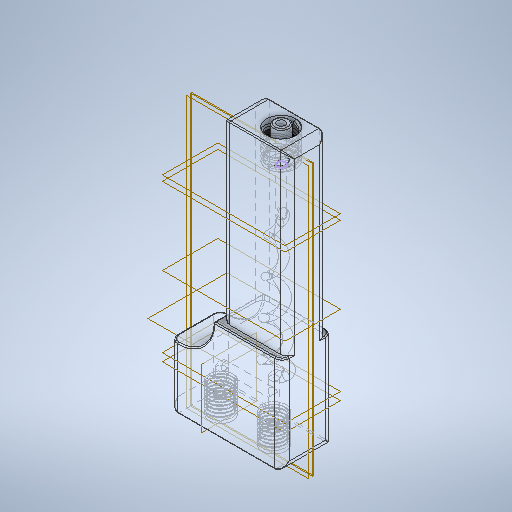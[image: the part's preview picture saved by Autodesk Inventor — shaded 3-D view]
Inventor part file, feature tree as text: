
AUTODESK INVENTOR PART (.ipt)
format: ipt  version: 2025 (Build 290162000, 162)  size: 1,340,416 bytes
history: native  units: mm
features: sketch x25, extrude x14, plane x11, other x7, revolve x6, fillet x3, projected_geometry x1
ambient origin geometry x8: Origin, YZ Plane, XZ Plane, XY Plane, X Axis, Y Axis, Z Axis, Center Point
bodies: Volumenkörper1 (feature_tree), Volumenkörper4 (feature_tree), Volumenkörper5 (feature_tree)
feature tree (67):
  extrude  "Extrusion1"  Depth=14.0mm
  extrude  "Extrusion2"  Depth=6.584mm
  plane  "Arbeitsebene4"
  extrude  "Extrusion3"  Depth=2.2mm
  extrude  "Extrusion8"  TaperAngle=0.0deg  [1 undecoded]
  revolve  "Umdrehung3"
  plane  "Arbeitsebene12"
  extrude  "Extrusion10"  Depth=5.0mm TaperAngle=0.0deg
  plane  "Arbeitsebene7"
  extrude  "Extrusion13"  Depth=2.2mm TaperAngle=0.0deg
  extrude  "Extrusion14"  Depth=2.8mm TaperAngle=0.0deg
  other  "Spirale2"
  revolve  "Umdrehung9"
  extrude  "Extrusion15"  Depth=11.0mm
  revolve  "Umdrehung10"
  extrude  "Extrusion16"  Depth=50.0mm TaperAngle=0.0deg
  sketch  "Skizze32"  dims[d91=5.818mm d92=8.0mm d93=-0.061087mm]
  plane  "Arbeitsebene14"
  revolve  "Umdrehung11"
  plane  "Arbeitsebene15"
  plane  "Arbeitsebene16"
  revolve  "Umdrehung12"
  plane  "Arbeitsebene17"
  extrude  "Extrusion19"  TaperAngle=90.0deg  [1 undecoded]
  extrude  "Extrusion20"  Depth=8.15mm
  revolve  "Umdrehung14"
  plane  "Arbeitsebene18"
  other  "Spirale3"
  fillet  "Rundung1"  Radius=13.6mm
  fillet  "Rundung2"  [1 undecoded]
  sketch  "Skizze44"  dims[d110=4.75mm]
  plane  "Arbeitsebene19"
  other  "Trennen1"
  other  "Körper verschieben1"
  extrude  "Extrusion21"  Depth=7.52mm
  other  "Kombinieren1"
  plane  "Arbeitsebene20"
  extrude  "Extrusion22"  Depth=8.0mm
  extrude  "Extrusion23"  Depth=1.1mm
  fillet  "Rundung4"  Radius=2.2mm
  plane  "Arbeitsebene21"
  other  "Spirale4"
  other  "Spirale5"
  sketch  "Skizze49"  dims[d117=0.318mm d125=5.0mm d126=10.0mm d127=12.5mm d128=0.061087mm d129=90.0deg d130=90.0deg d131=0.0mm d132=0.0mm d133=0.3mm d134=2.0mm d136=0.0mm d137=0.0mm d138=0.0mm d139=10.0mm d140=10.0mm d141=0.0mm d142=11.0mm d143=0.0mm d144=20.0mm d145=14.0mm d146=0.0mm d147=0.3mm d148=-1.1mm d156=0.897mm d157=10.0mm d158=73.0mm d159=0.0mm d160=90.0deg d161=90.0deg d162=0.0mm d163=0.0mm d170=0.897mm d171=10.0mm d172=73.0mm d173=0.0mm d174=90.0deg d175=90.0deg d176=0.0mm d177=0.0mm d22=0.5mm d23=0.872665mm d82=0.872665mm d83=0.5mm d95=0.5mm d96=0.872665mm d97=0.5mm d98=0.872665mm]
  sketch  "Skizze1"  dims[d0=31.0mm d1=14.0mm]
  sketch  "Skizze2"  dims[d2=11.0mm d3=0.0mm d4=6.584mm]
  sketch  "Skizze3"  dims[d6=8.0mm d7=0.0mm d8=2.2mm]
  sketch  "Skizze10"  dims[d9=2.2mm d11=0.0mm]
  sketch  "Skizze11"  dims[d12=8.0mm d13=0.0mm d24=5.0mm d25=0.0mm]
  sketch  "Skizze15"  dims[d26=90.0deg d33=2.2mm d34=0.0mm]
  sketch  "Skizze23"  dims[d35=13.2mm d60=2.8mm d61=0.0mm]
  sketch  "Skizze24"  dims[d62=18.0mm d63=11.0mm]
  sketch  "Skizze25"  dims[d64=1.5mm d65=50.0mm d66=0.0mm]
  sketch  "Skizze27"  dims[d70=8.75mm]
  sketch  "Skizze29"  dims[d71=10.0mm d72=10.0mm d73=35.0mm d74=-0.436332mm d75=90.0deg d76=90.0deg d77=0.0mm d78=0.0mm d80=90.0deg]
  sketch  "Skizze30"  dims[d81=5.9mm d84=8.15mm d86=13.6mm d87=0.0mm d88=90.0deg]
  sketch  "Skizze31"  dims[d89=8.13mm d90=7.52mm]
  sketch  "Skizze35"  dims[d100=0.0mm d102=1.1mm d103=2.2mm]
  sketch  "Skizze36"  dims[d105=90.0deg]
  sketch  "Skizze39"  dims[d106=54.45mm]
  sketch  "Skizze40"  dims[d107=8.37758mm]
  projected_geometry  "Projizierte Kontur2"
  sketch  "Skizze43"  dims[d108=1.55mm]
  sketch  "Skizze45"  dims[d111=9.0mm d112=-0.300197mm]
  sketch  "Skizze46"  dims[d113=2.2mm]
  sketch  "Skizze47"  dims[d114=12.5mm d115=0.0mm]
  sketch  "Skizze48"  dims[d116=8.552113mm]
note: 3 required parameter values undecoded (feature->parameter linkage not recoverable at this tier; creation-order binding heuristic only, values carry confidence <= 0.55)
